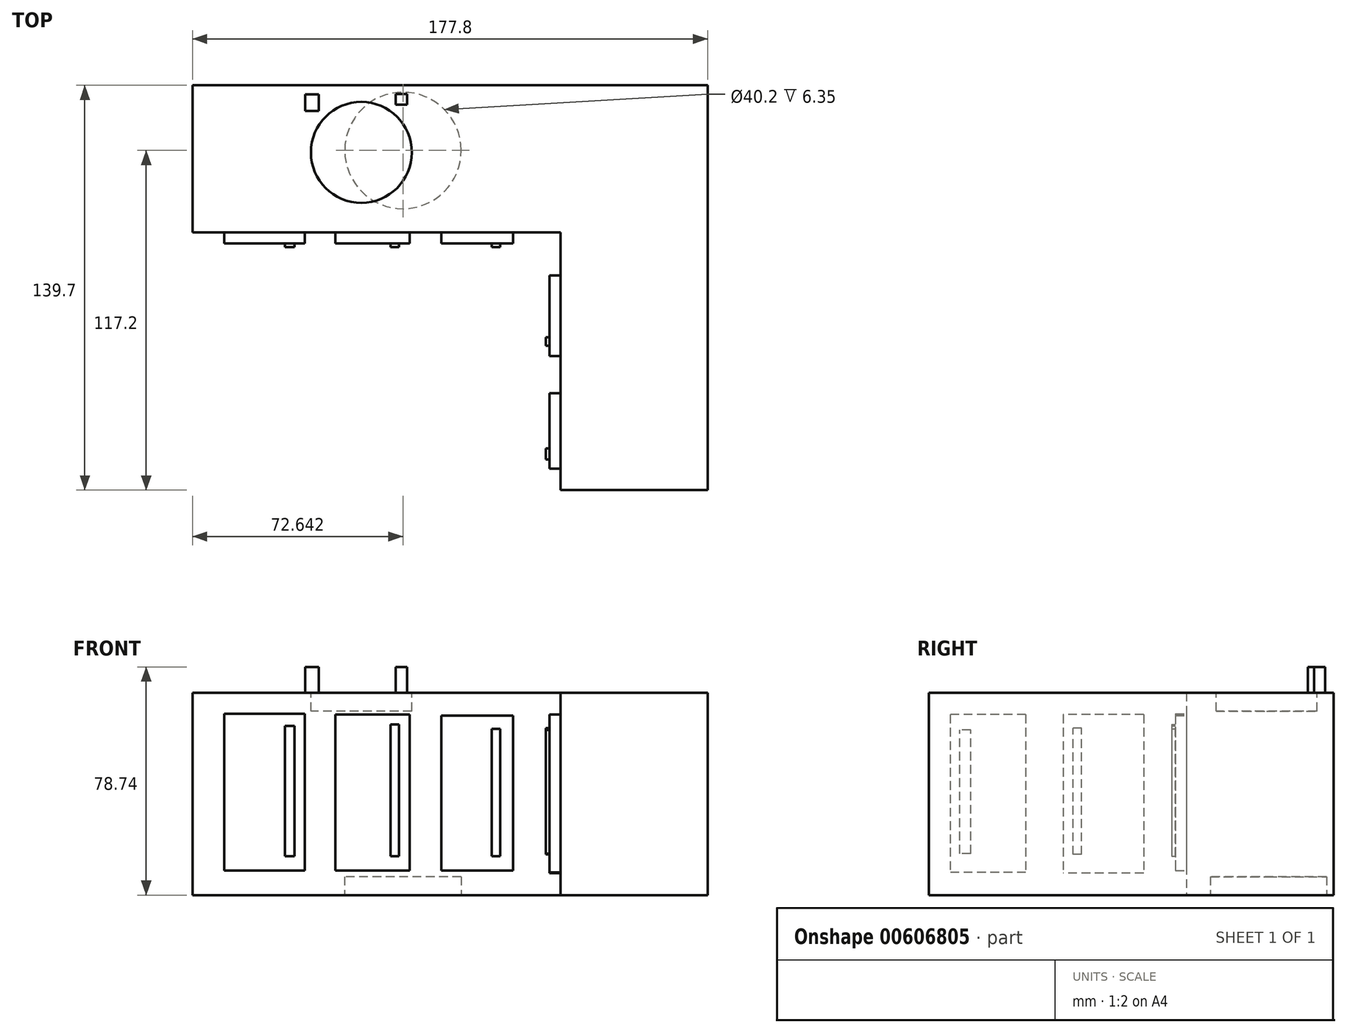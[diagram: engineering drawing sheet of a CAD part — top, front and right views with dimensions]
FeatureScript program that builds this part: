
annotation { "Feature Type Name" : "Feature", "Feature Type Description" : "" }
export const myFeature = defineFeature(function(context is Context, id is Id, definition is map)
    precondition{}
    {
        {
            var Q0;
            Q0=qCreatedBy(makeId("Top.planeOp"),FACE);
            var sketch = newSketch(context, id + "F0", { "sketchPlane" : qUnion([Q0])});
            skLineSegment(sketch, "E0.bottom", {"start": v(-90.51, 80.44) * mm, "end": v(87.29, 80.44) * mm});
            skLineSegment(sketch, "E0.top", {"start": v(-90.51, 29.64) * mm, "end": v(87.29, 29.64) * mm});
            skLineSegment(sketch, "E0.left", {"start": v(-90.51, 80.44) * mm, "end": v(-90.51, 29.64) * mm});
            skLineSegment(sketch, "E0.right", {"start": v(87.29, 80.44) * mm, "end": v(87.29, 29.64) * mm});
            skLineSegment(sketch, "E1.bottom", {"start": v(87.29, 29.64) * mm, "end": v(36.49, 29.64) * mm});
            skLineSegment(sketch, "E1.top", {"start": v(87.29, -59.26) * mm, "end": v(36.49, -59.26) * mm});
            skLineSegment(sketch, "E1.left", {"start": v(87.29, 29.64) * mm, "end": v(87.29, -59.26) * mm});
            skLineSegment(sketch, "E1.right", {"start": v(36.49, 29.64) * mm, "end": v(36.49, -59.26) * mm});
            skSolve(sketch);
        }
        {
            var Q0;
            Q0 = qSketchRegion(id + "F0", true);
            extrude(context, id + "F1", {"entities" : qUnion([Q0]), "depth" : 69.85 * mm, "offsetDistance" : 25.4 * mm});
        }
        {
            var Q0;
            Q0=qCreatedBy(makeId("Top.planeOp"),FACE);
            var sketch = newSketch(context, id + "F2", { "sketchPlane" : qUnion([Q0])});
            skCircle(sketch, "E2", {"center": v(-17.87, 57.94) * mm, "radius": 20.1 * mm});
            skSolve(sketch);
        }
        {
            var Q0;
            Q0 = qSketchRegion(id + "F2", true);
            extrude(context, id + "F3", {"entities" : qUnion([Q0]), "operationType" : NewBodyOperationType.REMOVE, "oppositeDirection" : true, "depth" : -6.35 * mm, "offsetDistance" : 25.4 * mm});
        }
        {
            var Q0;
            Q0=makeQuery(id+"F1.opExtrude","CAP_FACE",FACE,{"disambiguationData":[OSD([sQuery(id+"F0.wireOp",EDGE,"E0.bottom"),sQuery(id+"F0.wireOp",EDGE,"E0.top"),sQuery(id+"F0.wireOp",EDGE,"E0.left"),sQuery(id+"F0.wireOp",EDGE,"E0.right"),sQuery(id+"F0.wireOp",EDGE,"E1.top"),sQuery(id+"F0.wireOp",EDGE,"E1.left"),sQuery(id+"F0.wireOp",EDGE,"E1.right")])],"isStart":false});
            var sketch = newSketch(context, id + "F4", { "sketchPlane" : qUnion([Q0])});
            skCircle(sketch, "E3", {"center": v(-32.23, 57.3) * mm, "radius": 17.41 * mm});
            skSolve(sketch);
        }
        {
            var Q0;
            Q0 = qSketchRegion(id + "F4", true);
            extrude(context, id + "F5", {"entities" : qUnion([Q0]), "operationType" : NewBodyOperationType.REMOVE, "oppositeDirection" : true, "depth" : 6.35 * mm, "offsetDistance" : 25.4 * mm});
        }
        {
            var Q0;
            Q0=makeQuery(id+"F1.opExtrude","CAP_FACE",FACE,{"disambiguationData":[OSD([sQuery(id+"F0.wireOp",EDGE,"E0.bottom"),sQuery(id+"F0.wireOp",EDGE,"E0.top"),sQuery(id+"F0.wireOp",EDGE,"E0.left"),sQuery(id+"F0.wireOp",EDGE,"E0.right"),sQuery(id+"F0.wireOp",EDGE,"E1.top"),sQuery(id+"F0.wireOp",EDGE,"E1.left"),sQuery(id+"F0.wireOp",EDGE,"E1.right")])],"isStart":false});
            var sketch = newSketch(context, id + "F6", { "sketchPlane" : qUnion([Q0])});
            skLineSegment(sketch, "E4.bottom", {"start": v(-51.56, 77.25) * mm, "end": v(-46.96, 77.25) * mm});
            skLineSegment(sketch, "E4.top", {"start": v(-51.56, 71.58) * mm, "end": v(-46.96, 71.58) * mm});
            skLineSegment(sketch, "E4.left", {"start": v(-51.56, 77.25) * mm, "end": v(-51.56, 71.58) * mm});
            skLineSegment(sketch, "E4.right", {"start": v(-46.96, 77.25) * mm, "end": v(-46.96, 71.58) * mm});
            skLineSegment(sketch, "E5.bottom", {"start": v(-20.42, 77.46) * mm, "end": v(-16.41, 77.46) * mm});
            skLineSegment(sketch, "E5.top", {"start": v(-20.42, 73.7) * mm, "end": v(-16.41, 73.7) * mm});
            skLineSegment(sketch, "E5.left", {"start": v(-20.42, 77.46) * mm, "end": v(-20.42, 73.7) * mm});
            skLineSegment(sketch, "E5.right", {"start": v(-16.41, 77.46) * mm, "end": v(-16.41, 73.7) * mm});
            skSolve(sketch);
        }
        {
            var Q0;
            Q0 = qSketchRegion(id + "F6", true);
            extrude(context, id + "F7", {"entities" : qUnion([Q0]), "operationType" : NewBodyOperationType.ADD, "depth" : 8.9 * mm, "offsetDistance" : 25.4 * mm});
        }
        {
            var Q0;
            Q0=makeQuery(id+"F1.opExtrude","SWEPT_FACE",FACE,{"disambiguationData":[OSD([sQuery(id+"F0.wireOp",EDGE,"E0.top")])]});
            var sketch = newSketch(context, id + "F8", { "sketchPlane" : qUnion([Q0])});
            skLineSegment(sketch, "E6.bottom", {"start": v(-79.6, 62.57) * mm, "end": v(-51.8, 62.57) * mm});
            skLineSegment(sketch, "E6.top", {"start": v(-79.6, 8.44) * mm, "end": v(-51.8, 8.44) * mm});
            skLineSegment(sketch, "E6.left", {"start": v(-79.6, 62.57) * mm, "end": v(-79.6, 8.44) * mm});
            skLineSegment(sketch, "E6.right", {"start": v(-51.8, 62.57) * mm, "end": v(-51.8, 8.44) * mm});
            skLineSegment(sketch, "E7.bottom", {"start": v(-41.26, 62.28) * mm, "end": v(-15.51, 62.28) * mm});
            skLineSegment(sketch, "E7.top", {"start": v(-41.26, 8.44) * mm, "end": v(-15.51, 8.44) * mm});
            skLineSegment(sketch, "E7.left", {"start": v(-41.26, 62.28) * mm, "end": v(-41.26, 8.44) * mm});
            skLineSegment(sketch, "E7.right", {"start": v(-15.51, 62.28) * mm, "end": v(-15.51, 8.44) * mm});
            skLineSegment(sketch, "E8.bottom", {"start": v(-4.69, 61.99) * mm, "end": v(20.18, 61.99) * mm});
            skLineSegment(sketch, "E8.top", {"start": v(-4.69, 8.44) * mm, "end": v(20.18, 8.44) * mm});
            skLineSegment(sketch, "E8.left", {"start": v(-4.69, 61.99) * mm, "end": v(-4.69, 8.44) * mm});
            skLineSegment(sketch, "E8.right", {"start": v(20.18, 61.99) * mm, "end": v(20.18, 8.44) * mm});
            skSolve(sketch);
        }
        {
            var Q0;
            Q0 = qSketchRegion(id + "F8", true);
            extrude(context, id + "F9", {"entities" : qUnion([Q0]), "operationType" : NewBodyOperationType.ADD, "depth" : 3.8 * mm, "offsetDistance" : 25.4 * mm});
        }
        {
            var Q0;
            Q0=makeQuery(id+"F1.opExtrude","SWEPT_FACE",FACE,{"disambiguationData":[OSD([sQuery(id+"F0.wireOp",EDGE,"E1.right")])]});
            var sketch = newSketch(context, id + "F10", { "sketchPlane" : qUnion([Q0])});
            skLineSegment(sketch, "E9.bottom", {"start": v(-14.85, 62.28) * mm, "end": v(12.95, 62.28) * mm});
            skLineSegment(sketch, "E9.top", {"start": v(-14.85, 7.56) * mm, "end": v(12.95, 7.56) * mm});
            skLineSegment(sketch, "E9.left", {"start": v(-14.85, 62.28) * mm, "end": v(-14.85, 7.56) * mm});
            skLineSegment(sketch, "E9.right", {"start": v(12.95, 62.28) * mm, "end": v(12.95, 7.56) * mm});
            skLineSegment(sketch, "E10.bottom", {"start": v(25.82, 62.28) * mm, "end": v(51.86, 62.28) * mm});
            skLineSegment(sketch, "E10.top", {"start": v(25.82, 7.85) * mm, "end": v(51.86, 7.85) * mm});
            skLineSegment(sketch, "E10.left", {"start": v(25.82, 62.28) * mm, "end": v(25.82, 7.85) * mm});
            skLineSegment(sketch, "E10.right", {"start": v(51.86, 62.28) * mm, "end": v(51.86, 7.85) * mm});
            skSolve(sketch);
        }
        {
            var Q0;
            Q0 = qSketchRegion(id + "F10", true);
            extrude(context, id + "F11", {"entities" : qUnion([Q0]), "operationType" : NewBodyOperationType.ADD, "depth" : 3.8 * mm, "offsetDistance" : 25.4 * mm});
        }
        {
            var Q0;
            Q0=makeQuery(id+"F1.opExtrude","SWEPT_FACE",FACE,{"disambiguationData":[OSD([sQuery(id+"F0.wireOp",EDGE,"E0.top")])]});
            var sketch = newSketch(context, id + "F12", { "sketchPlane" : qUnion([Q0])});
            skLineSegment(sketch, "E11.bottom", {"start": v(-58.65, 58.4) * mm, "end": v(-55.35, 58.4) * mm});
            skLineSegment(sketch, "E11.top", {"start": v(-58.65, 13.35) * mm, "end": v(-55.35, 13.35) * mm});
            skLineSegment(sketch, "E11.left", {"start": v(-58.65, 58.4) * mm, "end": v(-58.65, 13.35) * mm});
            skLineSegment(sketch, "E11.right", {"start": v(-55.35, 58.4) * mm, "end": v(-55.35, 13.35) * mm});
            skLineSegment(sketch, "E12.bottom", {"start": v(-19.29, 58.92) * mm, "end": v(-22.15, 58.92) * mm});
            skLineSegment(sketch, "E12.top", {"start": v(-19.29, 13.35) * mm, "end": v(-22.15, 13.35) * mm});
            skLineSegment(sketch, "E12.left", {"start": v(-19.29, 58.92) * mm, "end": v(-19.29, 13.35) * mm});
            skLineSegment(sketch, "E12.right", {"start": v(-22.15, 58.92) * mm, "end": v(-22.15, 13.35) * mm});
            skLineSegment(sketch, "E13.bottom", {"start": v(15.65, 57.4) * mm, "end": v(12.77, 57.4) * mm});
            skLineSegment(sketch, "E13.top", {"start": v(15.65, 13.35) * mm, "end": v(12.77, 13.35) * mm});
            skLineSegment(sketch, "E13.left", {"start": v(15.65, 57.4) * mm, "end": v(15.65, 13.35) * mm});
            skLineSegment(sketch, "E13.right", {"start": v(12.77, 57.4) * mm, "end": v(12.77, 13.35) * mm});
            skSolve(sketch);
        }
        {
            var Q0;
            Q0 = qSketchRegion(id + "F12", true);
            extrude(context, id + "F13", {"entities" : qUnion([Q0]), "operationType" : NewBodyOperationType.ADD, "depth" : 5.08 * mm, "offsetDistance" : 25.4 * mm});
        }
        {
            var Q0;
            Q0=makeQuery(id+"F1.opExtrude","SWEPT_FACE",FACE,{"disambiguationData":[OSD([sQuery(id+"F0.wireOp",EDGE,"E1.right")])]});
            var sketch = newSketch(context, id + "F14", { "sketchPlane" : qUnion([Q0])});
            skLineSegment(sketch, "E14.bottom", {"start": v(9.44, 57.6) * mm, "end": v(6.51, 57.6) * mm});
            skLineSegment(sketch, "E14.top", {"start": v(9.44, 14) * mm, "end": v(6.51, 14) * mm});
            skLineSegment(sketch, "E14.left", {"start": v(9.44, 57.6) * mm, "end": v(9.44, 14) * mm});
            skLineSegment(sketch, "E14.right", {"start": v(6.51, 57.6) * mm, "end": v(6.51, 14) * mm});
            skLineSegment(sketch, "E15.bottom", {"start": v(48.65, 57.01) * mm, "end": v(44.84, 57.01) * mm});
            skLineSegment(sketch, "E15.top", {"start": v(48.65, 14.3) * mm, "end": v(44.84, 14.3) * mm});
            skLineSegment(sketch, "E15.left", {"start": v(48.65, 57.01) * mm, "end": v(48.65, 14.3) * mm});
            skLineSegment(sketch, "E15.right", {"start": v(44.84, 57.01) * mm, "end": v(44.84, 14.3) * mm});
            skSolve(sketch);
        }
        {
            var Q0;
            Q0 = qSketchRegion(id + "F14", true);
            extrude(context, id + "F15", {"entities" : qUnion([Q0]), "operationType" : NewBodyOperationType.ADD, "depth" : 5.08 * mm, "offsetDistance" : 25.4 * mm});
        }
    });
